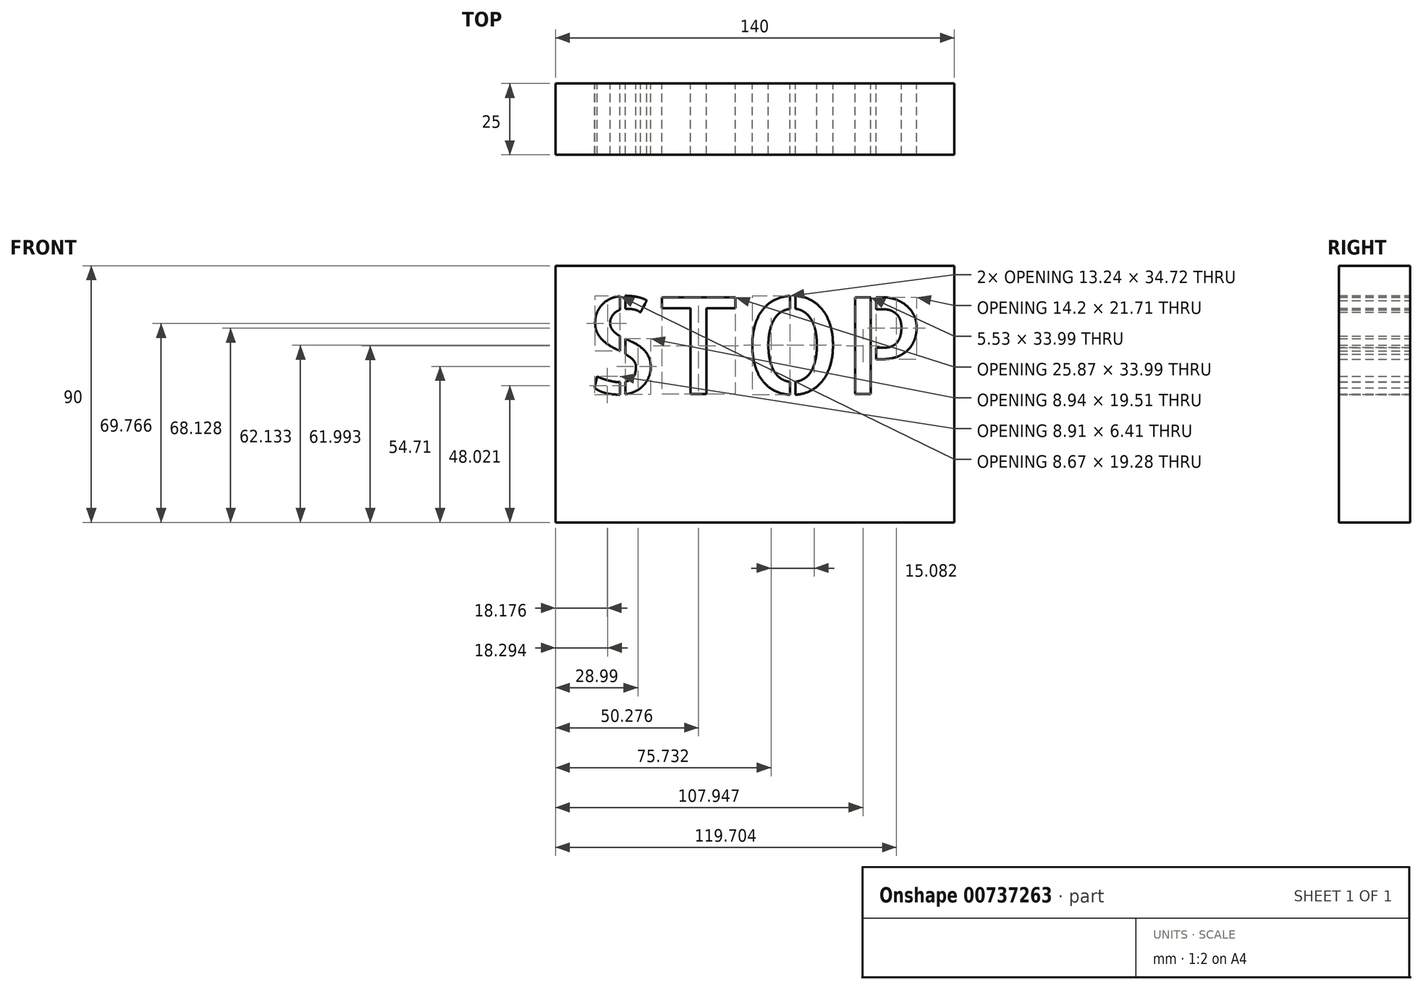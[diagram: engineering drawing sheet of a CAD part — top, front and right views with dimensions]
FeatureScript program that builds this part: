
annotation { "Feature Type Name" : "Feature", "Feature Type Description" : "" }
export const myFeature = defineFeature(function(context is Context, id is Id, definition is map)
    precondition{}
    {
        {
            var Q0;
            Q0=qCreatedBy(makeId("Front.planeOp"),FACE);
            var sketch = newSketch(context, id + "F0", { "sketchPlane" : qUnion([Q0])});
            skText(sketch, "E0", { "text": "STOP\n", "fontName": "AllertaStencil-Regular.ttf"});
            skLineSegment(sketch, "E1.bottom", {"start": v(-65.7, 179.12) * mm, "end": v(74.3, 179.12) * mm});
            skLineSegment(sketch, "E1.top", {"start": v(-65.7, 89.12) * mm, "end": v(74.3, 89.12) * mm});
            skLineSegment(sketch, "E1.left", {"start": v(-65.7, 179.12) * mm, "end": v(-65.7, 89.12) * mm});
            skLineSegment(sketch, "E1.right", {"start": v(74.3, 179.12) * mm, "end": v(74.3, 89.12) * mm});
            const initialGuessF0  = {"E0": [-0.0557, 0.13412, 1, 0, 0.034]};
            skSetInitialGuess(sketch, initialGuessF0);
            skSolve(sketch);
        }
        {
            var Q0;
            Q0 = qSketchRegion(id + "F0", true);
            extrude(context, id + "F1", {"entities" : qUnion([Q0]), "depth" : 25 * mm, "offsetDistance" : 25 * mm});
        }
    });
